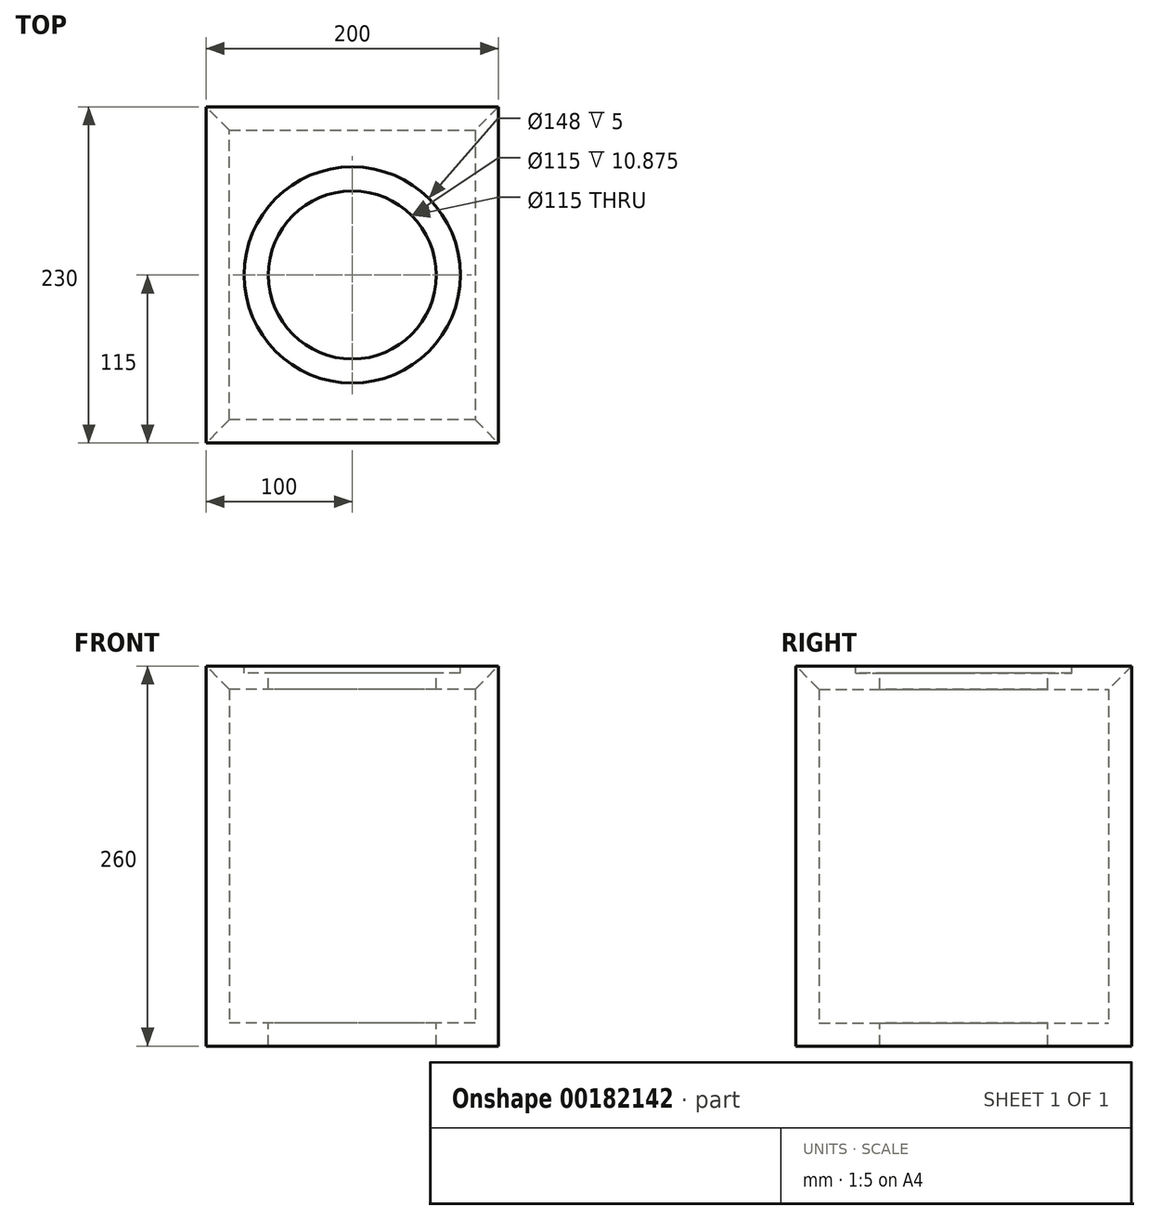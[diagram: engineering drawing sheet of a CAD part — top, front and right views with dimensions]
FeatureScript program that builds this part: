
annotation { "Feature Type Name" : "Feature", "Feature Type Description" : "" }
export const myFeature = defineFeature(function(context is Context, id is Id, definition is map)
    precondition{}
    {
        {
            var Q0;
            Q0=qCreatedBy(makeId("Top.planeOp"),FACE);
            var sketch = newSketch(context, id + "F0", { "sketchPlane" : qUnion([Q0])});
            skLineSegment(sketch, "E0.bottom", {"start": v(100, -115) * mm, "end": v(-100, -115) * mm});
            skLineSegment(sketch, "E0.top", {"start": v(100, 115) * mm, "end": v(-100, 115) * mm});
            skLineSegment(sketch, "E0.left", {"start": v(100, -115) * mm, "end": v(100, 115) * mm});
            skLineSegment(sketch, "E0.right", {"start": v(-100, -115) * mm, "end": v(-100, 115) * mm});
            skPoint(sketch, "E0.middle", {"position": v(0, 0) * mm});
            skSolve(sketch);
        }
        {
            var Q0;
            Q0=makeQuery(id+"F0.imprint","IMPRINT",FACE,{"disambiguationData":[TD([[makeQuery(id+"F0.imprint","IMPRINT",EDGE,{"derivedFrom":sQuery(id+"F0.wireOp",EDGE,"E0.bottom")}),-1.0]])]});
            extrude(context, id + "F1", {"entities" : qUnion([Q0]), "depth" : 260 * mm});
        }
        {
            var Q0;
            Q0=makeQuery(id+"F1.opExtrude","CAP_FACE",FACE,{"disambiguationData":[OSD([sQuery(id+"F0.wireOp",EDGE,"E0.bottom"),sQuery(id+"F0.wireOp",EDGE,"E0.top"),sQuery(id+"F0.wireOp",EDGE,"E0.left"),sQuery(id+"F0.wireOp",EDGE,"E0.right")])],"isStart":false});
            shell(context, id + "F2", {"entities" : qUnion([Q0]), "thickness" : 15.88 * mm});
        }
        {
            var Q0;
            {var subQ0=sQuery(id+"F0.wireOp",EDGE,"E0.right");Q0=makeQuery(id+"F2.opShell","OFFSET_EDGE",EDGE,{"disambiguationData":[OSD([subQ0]),TDD([makeQuery(id+"F1.opExtrude","CAP_EDGE",EDGE,{"disambiguationData":[OSD([subQ0])],"isStart":false})])]});}
            var Q1;
            {var subQ0=sQuery(id+"F0.wireOp",EDGE,"E0.top");Q1=makeQuery(id+"F2.opShell","OFFSET_EDGE",EDGE,{"disambiguationData":[OSD([subQ0]),TDD([makeQuery(id+"F1.opExtrude","CAP_EDGE",EDGE,{"disambiguationData":[OSD([subQ0])],"isStart":false})])]});}
            var Q2;
            {var subQ0=sQuery(id+"F0.wireOp",EDGE,"E0.left");Q2=makeQuery(id+"F2.opShell","OFFSET_EDGE",EDGE,{"disambiguationData":[OSD([subQ0]),TDD([makeQuery(id+"F1.opExtrude","CAP_EDGE",EDGE,{"disambiguationData":[OSD([subQ0])],"isStart":false})])]});}
            var Q3;
            {var subQ0=sQuery(id+"F0.wireOp",EDGE,"E0.bottom");Q3=makeQuery(id+"F2.opShell","OFFSET_EDGE",EDGE,{"disambiguationData":[OSD([subQ0]),TDD([makeQuery(id+"F1.opExtrude","CAP_EDGE",EDGE,{"disambiguationData":[OSD([subQ0])],"isStart":false})])]});}
            chamfer(context, id + "F3", {"entities" : qUnion([Q0, Q1, Q2, Q3]), "width" : 15.88 * mm, "tangentPropagation" : true});
        }
        {
            var Q0;
            {var subQ0=sQuery(id+"F0.wireOp",EDGE,"E0.right");Q0=makeQuery(id+"F3.opChamfer","BLEND_EDGE",EDGE,{"blendedFrom":[makeQuery(id+"F2.opShell","OFFSET_EDGE",EDGE,{"disambiguationData":[OSD([subQ0]),TDD([makeQuery(id+"F1.opExtrude","CAP_EDGE",EDGE,{"disambiguationData":[OSD([subQ0])],"isStart":false})])]}),makeQuery(id+"F1.opExtrude","SWEPT_FACE",FACE,{"disambiguationData":[OSD([subQ0])]})],"blendedInto":[makeQuery(id+"F1.opExtrude","SWEPT_FACE",FACE,{"disambiguationData":[OSD([subQ0])]})]});}
            cPoint(context, id + "F4", {"entities" : qUnion([Q0]), "parameter" : 0.5});
        }
        {
            var Q0;
            Q0=qCreatedBy(makeId("Top.planeOp"),FACE);
            var Q1;
            Q1 = qCreatedBy(id + "F4" ,VERTEX);
            cPlane(context, id + "F5", {"entities" : qUnion([Q0, Q1]), "cplaneType" : CPlaneType.PLANE_POINT, "offset" : 25.4 * mm, "width" : 152.4 * mm, "height" : 152.4 * mm});
        }
        {
            var Q0;
            Q0=qCreatedBy(id+"F5.planeOp",FACE);
            var sketch = newSketch(context, id + "F6", { "sketchPlane" : qUnion([Q0])});
            skLineSegment(sketch, "E1.0", {"start": v(100, -115) * mm, "end": v(100, 115) * mm, "construction": true});
            skLineSegment(sketch, "E2.0", {"start": v(100, 115) * mm, "end": v(-100, 115) * mm, "construction": true});
            skLineSegment(sketch, "E3.bottom", {"start": v(100, 115) * mm, "end": v(-100, 115) * mm});
            skLineSegment(sketch, "E3.top", {"start": v(100, -115) * mm, "end": v(-100, -115) * mm});
            skLineSegment(sketch, "E3.left", {"start": v(100, 115) * mm, "end": v(100, -115) * mm});
            skLineSegment(sketch, "E3.right", {"start": v(-100, 115) * mm, "end": v(-100, -115) * mm});
            skPoint(sketch, "E3.middle", {"position": v(0, 0) * mm});
            skSolve(sketch);
        }
        {
            var Q0;
            Q0=makeQuery(id+"F6.imprint","IMPRINT",FACE,{"disambiguationData":[TD([[makeQuery(id+"F6.imprint","IMPRINT",EDGE,{"derivedFrom":sQuery(id+"F6.wireOp",EDGE,"E3.bottom")}),1.0]])]});
            extrude(context, id + "F7", {"entities" : qUnion([Q0]), "oppositeDirection" : true, "depth" : 15.88 * mm});
        }
        {
            var Q0;
            Q0=makeQuery(id+"F7.opExtrude","CAP_EDGE",EDGE,{"disambiguationData":[OSD([sQuery(id+"F6.wireOp",EDGE,"E3.left")])],"isStart":false});
            var Q1;
            Q1=makeQuery(id+"F7.opExtrude","CAP_EDGE",EDGE,{"disambiguationData":[OSD([sQuery(id+"F6.wireOp",EDGE,"E3.top")])],"isStart":false});
            var Q2;
            Q2=makeQuery(id+"F7.opExtrude","CAP_EDGE",EDGE,{"disambiguationData":[OSD([sQuery(id+"F6.wireOp",EDGE,"E3.bottom")])],"isStart":false});
            var Q3;
            Q3=makeQuery(id+"F7.opExtrude","CAP_EDGE",EDGE,{"disambiguationData":[OSD([sQuery(id+"F6.wireOp",EDGE,"E3.right")])],"isStart":false});
            chamfer(context, id + "F8", {"entities" : qUnion([Q0, Q1, Q2, Q3]), "width" : 15.88 * mm, "tangentPropagation" : true});
        }
        {
            var Q0;
            Q0=makeQuery(id+"F7.opExtrude","CAP_FACE",FACE,{"disambiguationData":[OSD([sQuery(id+"F6.wireOp",EDGE,"E3.bottom"),sQuery(id+"F6.wireOp",EDGE,"E3.top"),sQuery(id+"F6.wireOp",EDGE,"E3.left"),sQuery(id+"F6.wireOp",EDGE,"E3.right")])],"isStart":true});
            var sketch = newSketch(context, id + "F9", { "sketchPlane" : qUnion([Q0])});
            skCircle(sketch, "E4", {"center": v(0, 0) * mm, "radius": 74 * mm});
            skSolve(sketch);
        }
        {
            var Q0;
            Q0=makeQuery(id+"F9.imprint","IMPRINT",FACE,{"disambiguationData":[TD([[makeQuery(id+"F9.imprint","IMPRINT",EDGE,{"derivedFrom":sQuery(id+"F9.wireOp",EDGE,"E4")}),1.0]])]});
            extrude(context, id + "F10", {"entities" : qUnion([Q0]), "operationType" : NewBodyOperationType.REMOVE, "oppositeDirection" : true, "depth" : 5 * mm});
        }
        {
            var Q0;
            Q0=makeQuery(id+"F10.boolean.opBoolean","COPY",FACE,{"derivedFrom":makeQuery(id+"F10.opExtrude","CAP_FACE",FACE,{"disambiguationData":[OSD([sQuery(id+"F9.wireOp",EDGE,"E4")])],"isStart":false})});
            var sketch = newSketch(context, id + "F11", { "sketchPlane" : qUnion([Q0])});
            skCircle(sketch, "E5", {"center": v(0, 0) * mm, "radius": 57.5 * mm});
            skSolve(sketch);
        }
        {
            var Q0;
            Q0=makeQuery(id+"F11.imprint","IMPRINT",FACE,{"disambiguationData":[TD([[makeQuery(id+"F11.imprint","IMPRINT",EDGE,{"derivedFrom":sQuery(id+"F11.wireOp",EDGE,"E5")}),1.0]])]});
            extrude(context, id + "F12", {"entities" : qUnion([Q0]), "operationType" : NewBodyOperationType.REMOVE, "endBound" : BoundingType.THROUGH_ALL, "oppositeDirection" : true, "depth" : 25.4 * mm});
        }
    });
